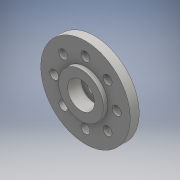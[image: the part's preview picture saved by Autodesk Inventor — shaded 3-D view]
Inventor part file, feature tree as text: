
AUTODESK INVENTOR PART (.ipt)
format: ipt  version: 2016 (Build 200138000, 138)  size: 153,600 bytes
history: native  units: mm
features: extrude x6, sketch x6, other x1
ambient origin geometry x8: Origin, YZ Plane, XZ Plane, XY Plane, X Axis, Y Axis, Z Axis, Center Point
bodies: Body1 (feature_tree)
feature tree (13):
  other  "ソリッド1"
  extrude  "押し出し1"  Depth=20.0mm
  extrude  "押し出し2"  Depth=2.0mm TaperAngle=0.0deg
  extrude  "押し出し3"  Depth=14.0mm
  extrude  "押し出し4"  Depth=2.0mm
  extrude  "押し出し5"  Depth=2.0mm
  extrude  "押し出し6"  Depth=2.0mm
  sketch  "スケッチ1"
  sketch  "スケッチ2"
  sketch  "スケッチ3"
  sketch  "スケッチ4"
  sketch  "スケッチ5"
  sketch  "スケッチ6"
